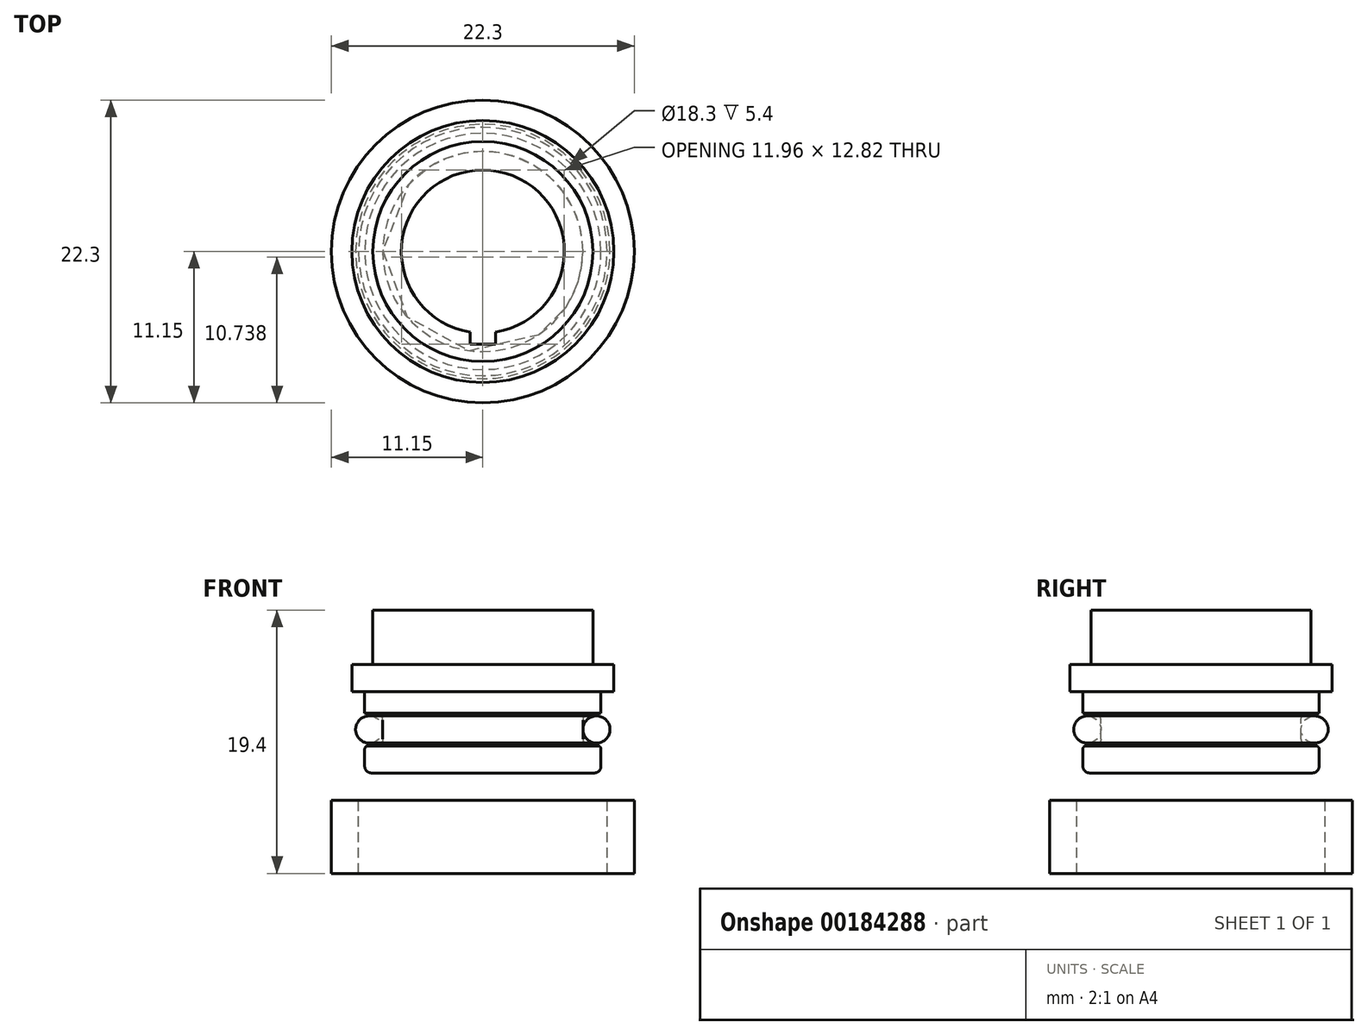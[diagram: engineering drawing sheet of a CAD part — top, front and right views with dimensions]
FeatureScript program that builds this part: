
annotation { "Feature Type Name" : "Feature", "Feature Type Description" : "" }
export const myFeature = defineFeature(function(context is Context, id is Id, definition is map)
    precondition{}
    {
        {
            var Q0;
            Q0=qCreatedBy(makeId("Front.planeOp"),FACE);
            var sketch = newSketch(context, id + "F0", { "sketchPlane" : qUnion([Q0])});
            skLineSegment(sketch, "E0", {"start": v(0, 24.07) * mm, "end": v(0, -25.12) * mm, "construction": true});
            skLineSegment(sketch, "E1", {"start": v(-6, 24.07) * mm, "end": v(-6, -25.12) * mm, "construction": true});
            skLineSegment(sketch, "E2.bottom", {"start": v(-8.7, 0) * mm, "end": v(-9.64, 0) * mm});
            skLineSegment(sketch, "E2.top", {"start": v(-6, 6) * mm, "end": v(-8.1, 6) * mm});
            skLineSegment(sketch, "E2.left", {"start": v(-6, 0) * mm, "end": v(-6, 6) * mm});
            skLineSegment(sketch, "E2.right", {"start": v(-9.64, 0) * mm, "end": v(-9.64, 2) * mm});
            skLineSegment(sketch, "E3.bottom", {"start": v(-6, -6) * mm, "end": v(-8.2, -6) * mm});
            skLineSegment(sketch, "E3.left", {"start": v(-6, -6) * mm, "end": v(-6, 0) * mm});
            skLineSegment(sketch, "E3.right", {"start": v(-8.7, -5.5) * mm, "end": v(-8.7, -4.25) * mm});
            skLineSegment(sketch, "E4.bottom", {"start": v(-8.7, -1.6) * mm, "end": v(-7.87, -1.6) * mm});
            skLineSegment(sketch, "E4.top", {"start": v(-8.45, -4) * mm, "end": v(-7.87, -4) * mm});
            skLineSegment(sketch, "E4.right", {"start": v(-7.37, -2.1) * mm, "end": v(-7.37, -3.5) * mm});
            skLineSegment(sketch, "E5.trimOffspring", {"start": v(-8.7, -1.6) * mm, "end": v(-8.7, 0) * mm});
            skCircle(sketch, "E6", {"center": v(-8.37, -2.8) * mm, "radius": 1 * mm});
            skPoint(sketch, "E7", {"position": v(-7.37, -2.8) * mm});
            skLineSegment(sketch, "E8", {"start": v(-7.37, -2.8) * mm, "end": v(-7.58, -2.8) * mm, "construction": true});
            skPoint(sketch, "E9.visualSharp", {"position": v(-7.37, -1.6) * mm});
            skArc(sketch, "E9.filletArc", {"start": v(-7.37, -2.1) * mm, "mid": v(-7.51, -1.75) * mm, "end": v(-7.87, -1.6) * mm});
            skPoint(sketch, "E10.visualSharp", {"position": v(-7.37, -4) * mm});
            skArc(sketch, "E10.filletArc", {"start": v(-7.87, -4) * mm, "mid": v(-7.51, -3.85) * mm, "end": v(-7.37, -3.5) * mm});
            skLineSegment(sketch, "E11.top", {"start": v(-9.64, 2) * mm, "end": v(-8.1, 2) * mm});
            skLineSegment(sketch, "E11.right", {"start": v(-8.1, 6) * mm, "end": v(-8.1, 2) * mm});
            skPoint(sketch, "E12.visualSharp", {"position": v(-8.7, -6) * mm});
            skArc(sketch, "E12.filletArc", {"start": v(-8.7, -5.5) * mm, "mid": v(-8.55, -5.85) * mm, "end": v(-8.2, -6) * mm});
            skLineSegment(sketch, "E13.bottom", {"start": v(-11.15, -8) * mm, "end": v(-9.15, -8) * mm});
            skLineSegment(sketch, "E13.top", {"start": v(-11.15, -13.4) * mm, "end": v(-9.15, -13.4) * mm});
            skLineSegment(sketch, "E13.left", {"start": v(-11.15, -8) * mm, "end": v(-11.15, -13.4) * mm});
            skLineSegment(sketch, "E13.right", {"start": v(-9.15, -8) * mm, "end": v(-9.15, -13.4) * mm});
            skPoint(sketch, "E14", {"position": v(-9.37, -2.8) * mm});
            skPoint(sketch, "E15.visualSharp", {"position": v(-8.7, -4) * mm});
            skArc(sketch, "E15.filletArc", {"start": v(-8.45, -4) * mm, "mid": v(-8.63, -4.07) * mm, "end": v(-8.7, -4.25) * mm});
            skSolve(sketch);
        }
        {
            var Q0;
            Q0=makeQuery(id+"F0.imprint","IMPRINT",FACE,{"disambiguationData":[TD([[makeQuery(id+"F0.imprint","IMPRINT",EDGE,{"derivedFrom":sQuery(id+"F0.wireOp",EDGE,"E2.bottom")}),-1.0]])]});
            var Q1;
            Q1=makeQuery(id+"F0.imprint","IMPRINT",FACE,{"disambiguationData":[TD([[makeQuery(id+"F0.imprint","IMPRINT",EDGE,{"derivedFrom":sQuery(id+"F0.wireOp",EDGE,"E6")}),1.0]])]});
            var Q2;
            Q2=makeQuery(id+"F0.imprint","IMPRINT",FACE,{"disambiguationData":[TD([[makeQuery(id+"F0.imprint","IMPRINT",EDGE,{"derivedFrom":sQuery(id+"F0.wireOp",EDGE,"KoJoLD7x-o5lw-8Brd-Qa1B-rJWSYuRxXGJb.bottom")}),1.0]])]});
            var Q3;
            Q3=makeQuery(id+"F0.imprint","IMPRINT",FACE,{"disambiguationData":[TD([[makeQuery(id+"F0.imprint","IMPRINT",EDGE,{"derivedFrom":sQuery(id+"F0.wireOp",EDGE,"E13.bottom")}),-1.0]])]});
            var Q4;
            Q4=sQuery(id+"F0.wireOp",EDGE,"E0");
            revolve(context, id + "F1", {"entities" : qUnion([Q0, Q1, Q2, Q3]), "axis" : qUnion([Q4]), "revolveType" : RevolveType.FULL});
        }
        {
            var Q0;
            Q0=makeQuery(id+"F1.opRevolve","SWEPT_FACE",FACE,{"disambiguationData":[OSD([sQuery(id+"F0.wireOp",EDGE,"E2.top")])]});
            var sketch = newSketch(context, id + "F2", { "sketchPlane" : qUnion([Q0])});
            skLineSegment(sketch, "E16", {"start": v(0, 8.1) * mm, "end": v(0, -8.1) * mm, "construction": true});
            skLineSegment(sketch, "E17", {"start": v(0, -8.1) * mm, "end": v(8.1, 0) * mm, "construction": true});
            skLineSegment(sketch, "E18", {"start": v(8.1, 0) * mm, "end": v(-8.1, 0) * mm, "construction": true});
            skLineSegment(sketch, "E19", {"start": v(-8.1, 0) * mm, "end": v(0, 8.1) * mm, "construction": true});
            skLineSegment(sketch, "E20", {"start": v(8.1, 0) * mm, "end": v(0, 8.1) * mm, "construction": true});
            skLineSegment(sketch, "E21", {"start": v(0, -8.1) * mm, "end": v(-8.1, 0) * mm, "construction": true});
            skLineSegment(sketch, "E22.bottom", {"start": v(-0.94, -6.82) * mm, "end": v(0.94, -6.82) * mm});
            skLineSegment(sketch, "E22.top", {"start": v(-0.94, -5.17) * mm, "end": v(0.94, -5.17) * mm});
            skLineSegment(sketch, "E22.left", {"start": v(-0.94, -6.82) * mm, "end": v(-0.94, -5.17) * mm});
            skLineSegment(sketch, "E22.right", {"start": v(0.94, -6.82) * mm, "end": v(0.94, -5.17) * mm});
            skPoint(sketch, "E22.middle", {"position": v(0, -6) * mm});
            skSolve(sketch);
        }
        {
            var Q0;
            {var subQ0=sQuery(id+"F2.wireOp",EDGE,"E22.bottom");Q0=makeQuery(id+"F2.imprint","IMPRINT",FACE,{"disambiguationData":[TD([[makeQuery(id+"F2.imprint","IMPRINT",EDGE,{"derivedFrom":subQ0}),1.0]])]});}
            var Q1;
            Q1=makeQuery(id+"F1.opRevolve","SWEPT_FACE",FACE,{"disambiguationData":[OSD([sQuery(id+"F0.wireOp",EDGE,"E3.bottom")])]});
            extrude(context, id + "F3", {"entities" : qUnion([Q0]), "operationType" : NewBodyOperationType.REMOVE, "endBound" : BoundingType.UP_TO_SURFACE, "oppositeDirection" : true, "endBoundEntityFace" : qUnion([Q1]), "depth" : 25 * mm});
        }
    });
